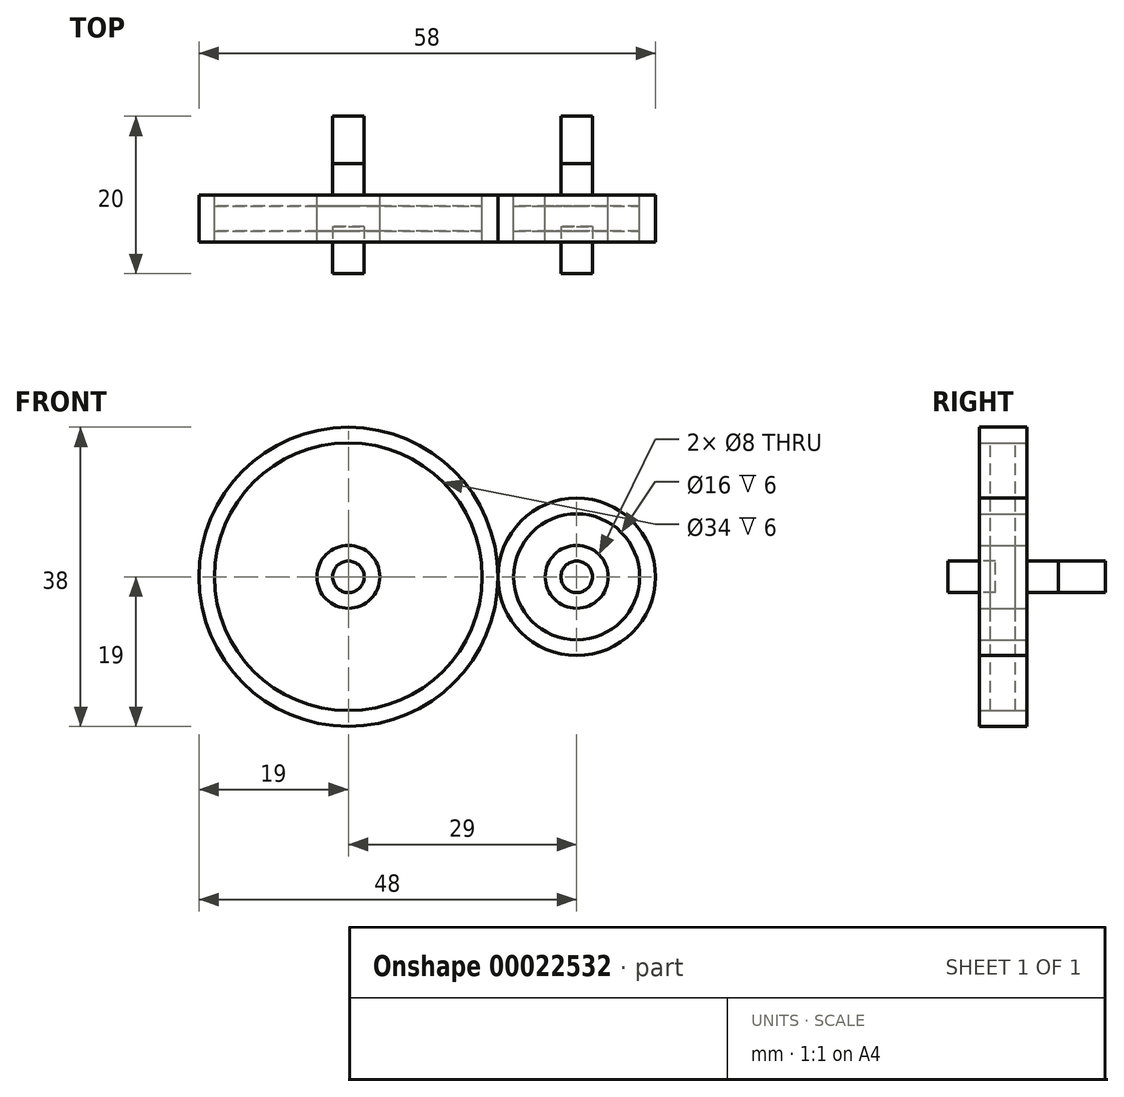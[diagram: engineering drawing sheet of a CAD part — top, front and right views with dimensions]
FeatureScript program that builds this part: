
annotation { "Feature Type Name" : "Feature", "Feature Type Description" : "" }
export const myFeature = defineFeature(function(context is Context, id is Id, definition is map)
    precondition{}
    {
        {
            var Q0;
            Q0=qCreatedBy(makeId("Front.planeOp"),FACE);
            var sketch = newSketch(context, id + "F0", { "sketchPlane" : qUnion([Q0])});
            skCircle(sketch, "E0", {"center": v(0, 0) * mm, "radius": 19 * mm});
            skCircle(sketch, "E1", {"center": v(0, 0) * mm, "radius": 17 * mm});
            skCircle(sketch, "E2", {"center": v(0, 0) * mm, "radius": 4 * mm});
            skCircle(sketch, "E3", {"center": v(0, 0) * mm, "radius": 2 * mm});
            skPoint(sketch, "E4.first.point", {"position": v(8.98, 16.74) * mm});
            skPoint(sketch, "E4.second.point", {"position": v(22.74, 29.52) * mm});
            skCircle(sketch, "E5", {"center": v(28.87, -2.72) * mm, "radius": 8 * mm});
            skCircle(sketch, "E6", {"center": v(28.87, -2.72) * mm, "radius": 4 * mm});
            skCircle(sketch, "E7", {"center": v(28.87, -2.72) * mm, "radius": 2 * mm});
            skCircle(sketch, "E8", {"center": v(28.87, -2.72) * mm, "radius": 10 * mm});
            skSolve(sketch);
        }
        {
            var Q0;
            Q0=makeQuery(id+"F0.imprint","IMPRINT",FACE,{"disambiguationData":[TD([[makeQuery(id+"F0.imprint","IMPRINT",EDGE,{"derivedFrom":sQuery(id+"F0.wireOp",EDGE,"E2")}),1.0]])]});
            var Q1;
            Q1=makeQuery(id+"F0.imprint","IMPRINT",FACE,{"disambiguationData":[TD([[makeQuery(id+"F0.imprint","IMPRINT",EDGE,{"derivedFrom":sQuery(id+"F0.wireOp",EDGE,"E0")}),1.0]])]});
            extrude(context, id + "F1", {"entities" : qUnion([Q0, Q1]), "endBound" : BoundingType.SYMMETRIC, "depth" : 6 * mm});
        }
        {
            var Q0;
            Q0=makeQuery(id+"F0.imprint","IMPRINT",FACE,{"disambiguationData":[TD([[makeQuery(id+"F0.imprint","IMPRINT",EDGE,{"derivedFrom":sQuery(id+"F0.wireOp",EDGE,"E1")}),1.0]])]});
            extrude(context, id + "F2", {"entities" : qUnion([Q0]), "endBound" : BoundingType.SYMMETRIC, "depth" : 3.17 * mm});
        }
        {
            var Q0;
            Q0=makeQuery(id+"F0.imprint","IMPRINT",FACE,{"disambiguationData":[TD([[makeQuery(id+"F0.imprint","IMPRINT",EDGE,{"derivedFrom":sQuery(id+"F0.wireOp",EDGE,"E3")}),1.0]])]});
            extrude(context, id + "F3", {"entities" : qUnion([Q0]), "operationType" : NewBodyOperationType.ADD, "endBound" : BoundingType.SYMMETRIC, "depth" : 14 * mm});
        }
        {
            var Q0;
            Q0=qCreatedBy(makeId("Front.planeOp"),FACE);
            var sketch = newSketch(context, id + "F4", { "sketchPlane" : qUnion([Q0])});
            skCircle(sketch, "E9", {"center": v(29, 0) * mm, "radius": 10 * mm});
            skCircle(sketch, "E10", {"center": v(29, 0) * mm, "radius": 8 * mm});
            skCircle(sketch, "E11", {"center": v(29, 0) * mm, "radius": 4 * mm});
            skCircle(sketch, "E12", {"center": v(29, 0) * mm, "radius": 2 * mm});
            skSolve(sketch);
        }
        {
            var Q0;
            Q0=makeQuery(id+"F4.imprint","IMPRINT",FACE,{"disambiguationData":[TD([[makeQuery(id+"F4.imprint","IMPRINT",EDGE,{"derivedFrom":sQuery(id+"F4.wireOp",EDGE,"E9")}),1.0]])]});
            var Q1;
            Q1=makeQuery(id+"F4.imprint","IMPRINT",FACE,{"disambiguationData":[TD([[makeQuery(id+"F4.imprint","IMPRINT",EDGE,{"derivedFrom":sQuery(id+"F4.wireOp",EDGE,"E11")}),1.0]])]});
            extrude(context, id + "F5", {"entities" : qUnion([Q0, Q1]), "operationType" : NewBodyOperationType.ADD, "endBound" : BoundingType.SYMMETRIC, "depth" : 6 * mm});
        }
        {
            var Q0;
            Q0=makeQuery(id+"F4.imprint","IMPRINT",FACE,{"disambiguationData":[TD([[makeQuery(id+"F4.imprint","IMPRINT",EDGE,{"derivedFrom":sQuery(id+"F4.wireOp",EDGE,"E10")}),1.0]])]});
            extrude(context, id + "F6", {"entities" : qUnion([Q0]), "endBound" : BoundingType.SYMMETRIC, "depth" : 3.17 * mm});
        }
        {
            var Q0;
            Q0=makeQuery(id+"F4.imprint","IMPRINT",FACE,{"disambiguationData":[TD([[makeQuery(id+"F4.imprint","IMPRINT",EDGE,{"derivedFrom":sQuery(id+"F4.wireOp",EDGE,"E12")}),1.0]])]});
            extrude(context, id + "F7", {"entities" : qUnion([Q0]), "operationType" : NewBodyOperationType.ADD, "endBound" : BoundingType.SYMMETRIC, "depth" : 14 * mm});
        }
        {
            var Q0;
            Q0=makeQuery(id+"F3.opExtrude","CAP_FACE",FACE,{"disambiguationData":[OSD([sQuery(id+"F0.wireOp",EDGE,"E3")])],"isStart":true});
            var Q1;
            Q1=makeQuery(id+"F7.opExtrude","CAP_FACE",FACE,{"disambiguationData":[OSD([sQuery(id+"F4.wireOp",EDGE,"E12")])],"isStart":true});
            var Q2;
            Q2=makeQuery(id+"F3.opExtrude","CAP_FACE",FACE,{"disambiguationData":[OSD([sQuery(id+"F0.wireOp",EDGE,"E3")])],"isStart":false});
            var Q3;
            Q3=makeQuery(id+"F7.opExtrude","CAP_FACE",FACE,{"disambiguationData":[OSD([sQuery(id+"F4.wireOp",EDGE,"E12")])],"isStart":false});
            extrude(context, id + "F8", {"entities" : qUnion([Q0, Q1, Q2, Q3]), "depth" : 6 * mm});
        }
    });
